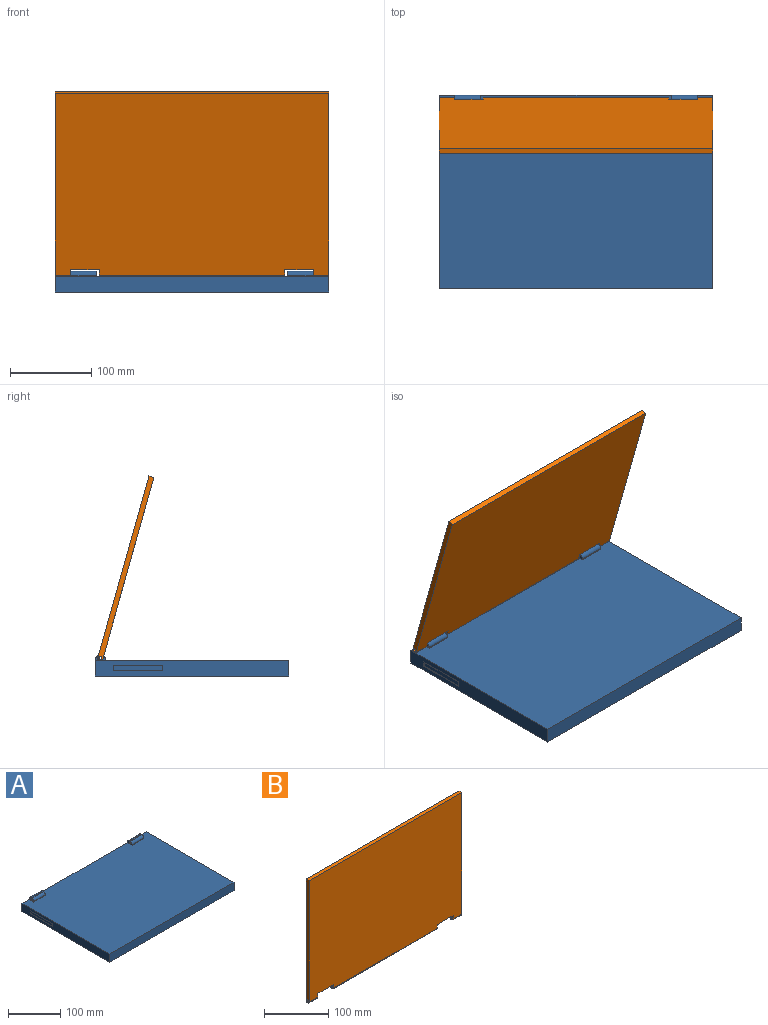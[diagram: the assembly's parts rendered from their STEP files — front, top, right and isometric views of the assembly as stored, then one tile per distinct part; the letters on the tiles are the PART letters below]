
ASSEMBLY  parts=2 mates=1
PART A: 65 faces, bbox 336.6x238.1x25.4 mm
  f0: plane 238.13x19.05mm, normal (-1,0,0), area 4153.2mm2, adj f1,f3,f4,f5,f60,f61,f62,f63
  f1: plane 336.55x20.32mm, normal (0,1,0), area 5975.6mm2, adj f0,f2,f3,f5,f6,f8,f10,f12
  f2: plane 238.13x19.05mm, normal (1,0,0), area 4455.6mm2, adj f1,f3,f4,f5,f20,f21,f22,f23
  f3: plane 336.55x238.13mm, normal (0,0,1), area 79334.5mm2, adj f0,f1,f2,f4,f6,f7,f8,f10
  f4: plane 336.55x19.05mm, normal (0,-1,0), area 6411.3mm2, adj f0,f2,f3,f5
  f5: plane 336.55x238.13mm, normal (0,0,-1), area 80141mm2, adj f0,f1,f2,f4
  f6: plane 12.7x6.35mm, normal (-1,0,0), area 58.2mm2, adj f1,f3,f7,f9,f15,f18,f19
  f7: plane 31.75x1.27mm, normal (0,-1,0), area 40.3mm2, adj f3,f6,f8,f18
  f8: plane 12.7x6.35mm, normal (1,0,0), area 58.2mm2, adj f1,f3,f7,f9,f15,f18,f19
  f9: plane 31.75x2.54mm, normal (0,0,1), area 80.6mm2, adj f6,f8,f18,f19
  f10: plane 12.7x6.35mm, normal (-1,0,0), area 58.2mm2, adj f1,f3,f11,f13,f14,f16,f17
  f11: plane 31.75x1.27mm, normal (0,-1,0), area 40.3mm2, adj f3,f10,f12,f16
  f12: plane 12.7x6.35mm, normal (1,0,0), area 58.2mm2, adj f1,f3,f11,f13,f14,f16,f17
  f13: plane 31.75x2.54mm, normal (0,0,1), area 80.6mm2, adj f10,f12,f16,f17
  f14: cylinder r=1.91mm len=31.75mm, axis (1,0,0), area 380mm2, adj f10,f12
  f15: cylinder r=1.91mm len=31.75mm, axis (1,0,0), area 380mm2, adj f6,f8
  f16: cylinder r=5.08mm len=31.75mm, axis (-1,0,0), area 253.4mm2, adj f10,f11,f12,f13
  f17: cylinder r=5.08mm len=31.75mm, axis (1,0,0), area 253.4mm2, adj f1,f10,f12,f13
  f18: cylinder r=5.08mm len=31.75mm, axis (-1,0,0), area 253.4mm2, adj f6,f7,f8,f9
  f19: cylinder r=5.08mm len=31.75mm, axis (1,0,0), area 253.4mm2, adj f1,f6,f8,f9
  f20: plane 12.7x12.7mm, normal (0,0,-1), area 161.3mm2, adj f2,f21,f23,f24
  f21: plane 12.7x6.35mm, normal (0,1,0), area 80.6mm2, adj f2,f20,f22,f24
  f22: plane 12.7x12.7mm, normal (0,0,1), area 161.3mm2, adj f2,f21,f23,f24
  f23: plane 12.7x6.35mm, normal (0,-1,0), area 80.6mm2, adj f2,f20,f22,f24
  f24: plane 12.7x6.35mm, normal (1,0,0), area 80.6mm2, adj f20,f21,f22,f23
  f25: cylinder r=3.97mm len=12.7mm, axis (0,1,0), area 316.7mm2, adj f1,f26
  f26: plane 7.94x7.94mm, normal (0,1,0), area 49.5mm2, adj f25
  f27: plane 12.7x3.18mm, normal (-1,0,0), area 40.3mm2, adj f1,f28,f34,f35
  f28: plane 12.7x0.79mm, normal (0,0,1), area 10.1mm2, adj f1,f27,f29,f35
  f29: plane 12.7x3.97mm, normal (-0.71,0,0.71), area 71.3mm2, adj f1,f28,f30,f35
  f30: plane 12.7x9.53mm, normal (0,0,1), area 121mm2, adj f1,f29,f31,f35
  f31: plane 12.7x3.97mm, normal (0.71,0,0.71), area 71.3mm2, adj f1,f30,f32,f35
  f32: plane 12.7x0.79mm, normal (0,0,1), area 10.1mm2, adj f1,f31,f33,f35
  f33: plane 12.7x3.18mm, normal (1,0,0), area 40.3mm2, adj f1,f32,f34,f35
  f34: plane 19.05x12.7mm, normal (0,0,-1), area 241.9mm2, adj f1,f27,f33,f35
  f35: plane 19.05x7.14mm, normal (0,1,0), area 114mm2, adj f27,f28,f29,f30,f31,f32,f33,f34
  f36: plane 12.7x12.7mm, normal (0,0,-1), area 161.3mm2, adj f1,f37,f39,f40
  f37: plane 12.7x6.35mm, normal (-1,0,0), area 80.6mm2, adj f1,f36,f38,f40
  f38: plane 12.7x12.7mm, normal (0,0,1), area 161.3mm2, adj f1,f37,f39,f40
  f39: plane 12.7x6.35mm, normal (1,0,0), area 80.6mm2, adj f1,f36,f38,f40
  f40: plane 12.7x6.35mm, normal (0,1,0), area 80.6mm2, adj f36,f37,f38,f39
  f41: plane 12.7x9.53mm, normal (0,0,-1), area 121mm2, adj f1,f42,f44,f45
  f42: plane 12.7x6.35mm, normal (-1,0,0), area 80.6mm2, adj f1,f41,f43,f45
  f43: plane 12.7x9.53mm, normal (0,0,1), area 121mm2, adj f1,f42,f44,f45
  f44: plane 12.7x6.35mm, normal (1,0,0), area 80.6mm2, adj f1,f41,f43,f45
  f45: plane 9.53x6.35mm, normal (0,1,0), area 60.5mm2, adj f41,f42,f43,f44
  f46: plane 12.7x6.35mm, normal (-1,0,0), area 80.6mm2, adj f1,f47,f49,f50
  f47: plane 12.7x12.7mm, normal (0,0,1), area 161.3mm2, adj f1,f46,f48,f50
  f48: plane 12.7x6.35mm, normal (1,0,0), area 80.6mm2, adj f1,f47,f49,f50
  f49: plane 12.7x12.7mm, normal (0,0,-1), area 161.3mm2, adj f1,f46,f48,f50
  f50: plane 12.7x6.35mm, normal (0,1,0), area 80.6mm2, adj f46,f47,f48,f49
  f51: plane 12.7x9.53mm, normal (-1,0,0), area 121mm2, adj f1,f52,f58,f59
  f52: plane 12.7x12.7mm, normal (0,0,1), area 161.3mm2, adj f1,f51,f53,f59
  f53: plane 12.7x9.53mm, normal (1,0,0), area 121mm2, adj f1,f52,f54,f59
  f54: plane 12.7x3.18mm, normal (0,0,-1), area 40.3mm2, adj f1,f53,f55,f59
  f55: plane 12.7x1.59mm, normal (1,0,0), area 20.2mm2, adj f1,f54,f56,f59
  f56: plane 12.7x6.35mm, normal (0,0,-1), area 80.6mm2, adj f1,f55,f57,f59
  f57: plane 12.7x1.59mm, normal (-1,0,0), area 20.2mm2, adj f1,f56,f58,f59
  f58: plane 12.7x3.18mm, normal (0,0,-1), area 40.3mm2, adj f1,f51,f57,f59
  f59: plane 12.7x11.11mm, normal (0,1,0), area 131mm2, adj f51,f52,f53,f54,f55,f56,f57,f58
  f60: plane 60.33x0.79mm, normal (0,0,-1), area 47.9mm2, adj f0,f61,f63,f64
  f61: plane 6.35x0.79mm, normal (0,-1,0), area 5mm2, adj f0,f60,f62,f64
  f62: plane 60.33x0.79mm, normal (0,0,1), area 47.9mm2, adj f0,f61,f63,f64
  f63: plane 6.35x0.79mm, normal (0,1,0), area 5mm2, adj f0,f60,f62,f64
  f64: plane 60.33x6.35mm, normal (-1,0,0), area 383.1mm2, adj f60,f61,f62,f63
PART B: 23 faces, bbox 336.6x6.4x235 mm
  f0: plane 234.95x6.35mm, normal (-1,0,0), area 1477.8mm2, adj f1,f11,f12,f13,f16,f19,f22
  f1: plane 19.05x1.27mm, normal (0,0,-1), area 24.2mm2, adj f0,f2,f19,f22
  f2: plane 9.53x6.35mm, normal (1,0,0), area 46.3mm2, adj f1,f3,f12,f13,f16,f19,f22
  f3: plane 34.93x6.35mm, normal (0,0,-1), area 221.8mm2, adj f2,f4,f12,f13
  f4: plane 9.53x6.35mm, normal (-1,0,0), area 46.3mm2, adj f3,f5,f12,f13,f15,f18,f21
  f5: plane 228.6x1.27mm, normal (0,0,-1), area 290.3mm2, adj f4,f6,f18,f21
  f6: plane 9.53x6.35mm, normal (1,0,0), area 46.3mm2, adj f5,f7,f12,f13,f15,f18,f21
  f7: plane 34.93x6.35mm, normal (0,0,-1), area 221.8mm2, adj f6,f8,f12,f13
  f8: plane 9.53x6.35mm, normal (-1,0,0), area 46.3mm2, adj f7,f9,f12,f13,f14,f17,f20
  f9: plane 19.05x1.27mm, normal (0,0,-1), area 24.2mm2, adj f8,f10,f17,f20
  f10: plane 234.95x6.35mm, normal (1,0,0), area 1477.8mm2, adj f9,f11,f12,f13,f14,f17,f20
  f11: plane 336.55x6.35mm, normal (0,0,1), area 2137.1mm2, adj f0,f10,f12,f13
  f12: plane 336.55x232.41mm, normal (0,-1,0), area 77729.7mm2, adj f0,f2,f3,f4,f6,f7,f8,f10
  f13: plane 336.55x232.41mm, normal (0,1,0), area 77729.7mm2, adj f0,f2,f3,f4,f6,f7,f8,f10
  f14: cylinder r=1.91mm len=19.05mm, axis (1,0,0), area 228mm2, adj f8,f10
  f15: cylinder r=1.91mm len=228.6mm, axis (1,0,0), area 2736.2mm2, adj f4,f6
  f16: cylinder r=1.91mm len=19.05mm, axis (1,0,0), area 228mm2, adj f0,f2
  f17: cylinder r=2.54mm len=19.05mm, axis (1,0,0), area 76mm2, adj f8,f9,f10,f13
  f18: cylinder r=2.54mm len=228.6mm, axis (1,0,0), area 912.1mm2, adj f4,f5,f6,f13
  f19: cylinder r=2.54mm len=19.05mm, axis (1,0,0), area 76mm2, adj f0,f1,f2,f13
  f20: cylinder r=2.54mm len=19.05mm, axis (-1,0,0), area 76mm2, adj f8,f9,f10,f12
  f21: cylinder r=2.54mm len=228.6mm, axis (-1,0,0), area 912.1mm2, adj f4,f5,f6,f12
  f22: cylinder r=2.54mm len=19.05mm, axis (-1,0,0), area 76mm2, adj f0,f1,f2,f12
PLACE A t=(0,0,-19.05)mm
PLACE B rot(axis=(1,0,0),15.7deg) t=(0,-2.43,0.98)mm
MATE revolute A.f14 <-> B.f14  axis (-1,0,0) through (19.05,-6.35,3.18)mm
